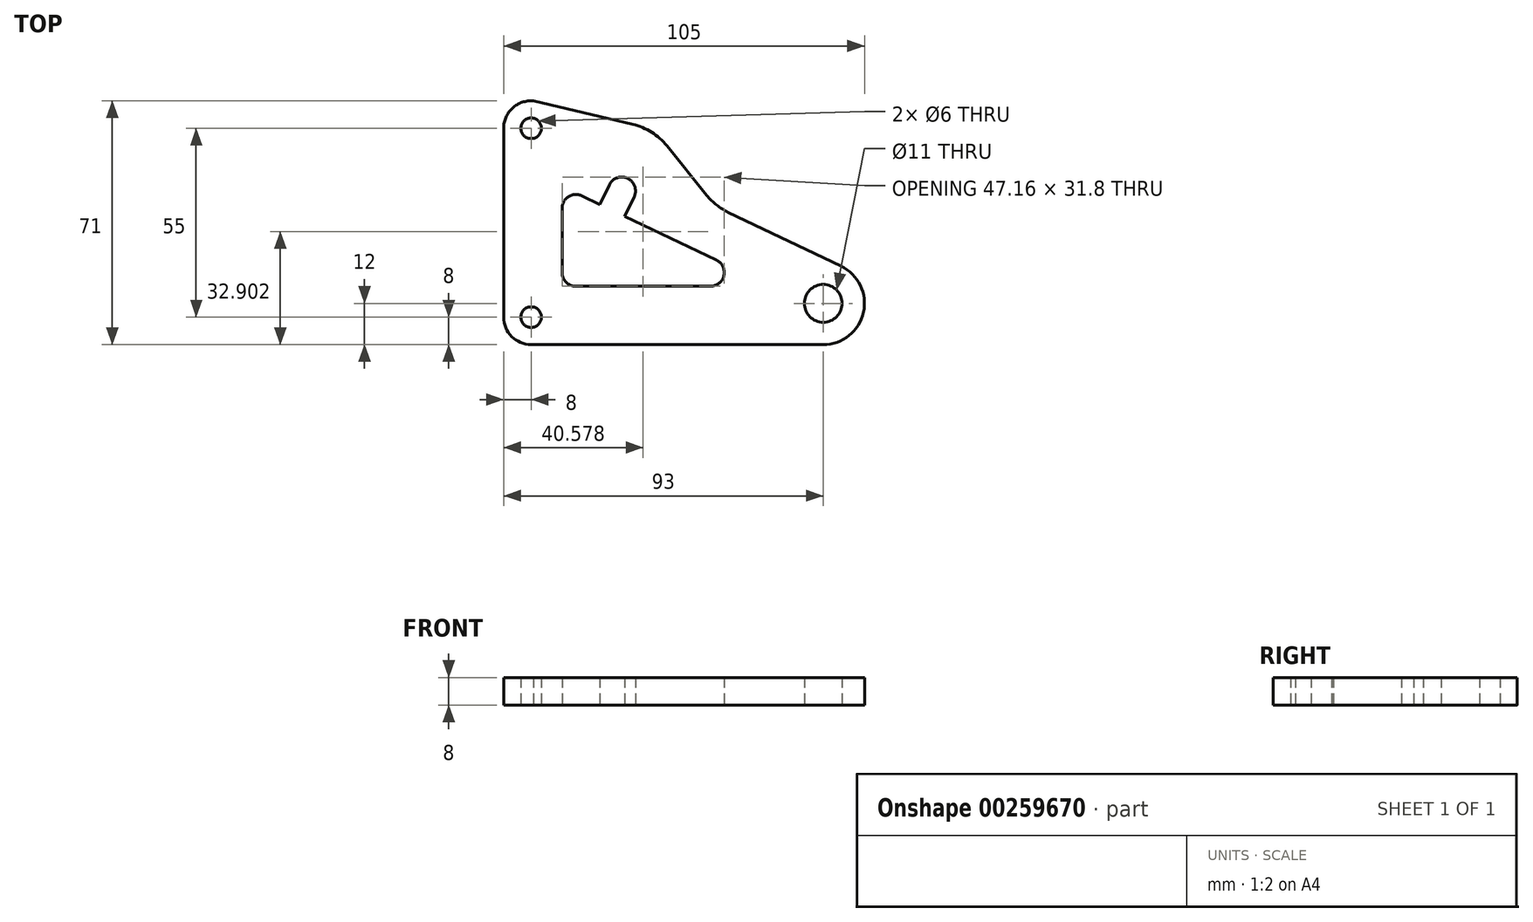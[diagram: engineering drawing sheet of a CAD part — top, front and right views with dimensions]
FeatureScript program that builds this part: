
annotation { "Feature Type Name" : "Feature", "Feature Type Description" : "" }
export const myFeature = defineFeature(function(context is Context, id is Id, definition is map)
    precondition{}
    {
        {
            var Q0;
            Q0=qCreatedBy(makeId("Top.planeOp"),FACE);
            var sketch = newSketch(context, id + "F0", { "sketchPlane" : qUnion([Q0])});
            skLineSegment(sketch, "E0", {"start": v(0, 63) * mm, "end": v(0, 8) * mm});
            skLineSegment(sketch, "E1", {"start": v(8, 0) * mm, "end": v(93, 0) * mm});
            skArc(sketch, "E2", {"start": v(93, 0) * mm, "mid": v(104.7, 9.35) * mm, "end": v(98.18, 22.83) * mm});
            skCircle(sketch, "E3", {"center": v(8, 8) * mm, "radius": 3 * mm});
            skCircle(sketch, "E4", {"center": v(8, 63) * mm, "radius": 3 * mm});
            skLineSegment(sketch, "E5", {"start": v(17, 39.73) * mm, "end": v(17, 21) * mm});
            skLineSegment(sketch, "E6", {"start": v(21, 17) * mm, "end": v(60.18, 17) * mm});
            skLineSegment(sketch, "E7", {"start": v(61.9, 24.6) * mm, "end": v(35.23, 37.36) * mm});
            skCircle(sketch, "E8", {"center": v(93, 12) * mm, "radius": 5.5 * mm});
            skPoint(sketch, "E9.visualSharp", {"position": v(0, 71.72) * mm});
            skArc(sketch, "E9.filletArc", {"start": v(8.69, 70.97) * mm, "mid": v(2.6, 68.9) * mm, "end": v(0, 63) * mm});
            skPoint(sketch, "E10.visualSharp", {"position": v(0, 0) * mm});
            skArc(sketch, "E10.filletArc", {"start": v(0, 8) * mm, "mid": v(2.34, 2.34) * mm, "end": v(8, 0) * mm});
            skPoint(sketch, "E11.visualSharp", {"position": v(43.62, 62.73) * mm});
            skPoint(sketch, "E12.visualSharp", {"position": v(17, 17) * mm});
            skArc(sketch, "E12.filletArc", {"start": v(17, 21) * mm, "mid": v(18.17, 18.17) * mm, "end": v(21, 17) * mm});
            skPoint(sketch, "E13.visualSharp", {"position": v(17, 46.08) * mm});
            skArc(sketch, "E13.filletArc", {"start": v(22.73, 43.34) * mm, "mid": v(18.87, 43.11) * mm, "end": v(17, 39.73) * mm});
            skPoint(sketch, "E14.visualSharp", {"position": v(77.82, 17) * mm});
            skArc(sketch, "E14.filletArc", {"start": v(60.18, 17) * mm, "mid": v(64.08, 20.12) * mm, "end": v(61.9, 24.6) * mm});
            skPoint(sketch, "E15.visualSharp", {"position": v(61.67, 40.28) * mm});
            skArc(sketch, "E16", {"start": v(37.97, 43.08) * mm, "mid": v(36.08, 48.42) * mm, "end": v(30.75, 46.54) * mm});
            skCircle(sketch, "E17", {"center": v(34.36, 44.81) * mm, "radius": 7.5 * mm, "construction": true});
            skLineSegment(sketch, "E18", {"start": v(30.75, 46.54) * mm, "end": v(28.01, 40.81) * mm});
            skLineSegment(sketch, "E19", {"start": v(37.97, 43.08) * mm, "end": v(35.23, 37.36) * mm});
            skLineSegment(sketch, "E20.trimOffspring", {"start": v(28.01, 40.81) * mm, "end": v(22.73, 43.34) * mm});
            skPoint(sketch, "E21.orphan", {"position": v(34.36, 40.81) * mm});
            skLineSegment(sketch, "E22", {"start": v(98.18, 22.83) * mm, "end": v(61.67, 40.28) * mm});
            skLineSegment(sketch, "E23", {"start": v(43.62, 62.73) * mm, "end": v(8.69, 70.97) * mm});
            skLineSegment(sketch, "E24", {"start": v(43.62, 62.73) * mm, "end": v(61.67, 40.28) * mm});
            skSolve(sketch);
        }
        {
            var Q0;
            Q0 = qSketchRegion(id + "F0", true);
            extrude(context, id + "F1", {"entities" : qUnion([Q0]), "depth" : 8 * mm, "offsetDistance" : 25 * mm});
        }
        {
            var Q0;
            Q0=makeQuery(id+"F1.opExtrude","SWEPT_EDGE",EDGE,{"disambiguationData":[OSD([sQuery(id+"F0.wireOp",EDGE,"E23"),sQuery(id+"F0.wireOp",EDGE,"E24")])]});
            var Q1;
            Q1=makeQuery(id+"F1.opExtrude","SWEPT_EDGE",EDGE,{"disambiguationData":[OSD([sQuery(id+"F0.wireOp",EDGE,"E22"),sQuery(id+"F0.wireOp",EDGE,"E24")])]});
            fillet(context, id + "F2", {"entities" : qUnion([Q0, Q1]), "radius" : 18 * mm, "tangentPropagation" : true, "allowEdgeOverflow" : false});
        }
    });
